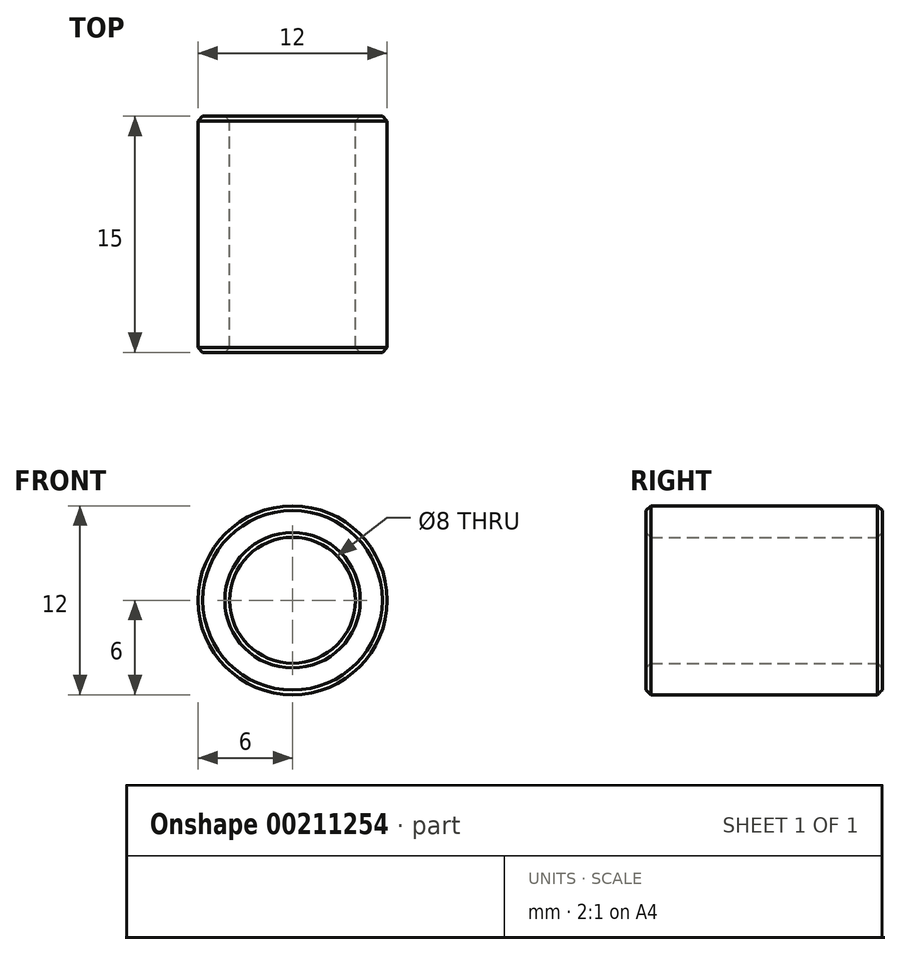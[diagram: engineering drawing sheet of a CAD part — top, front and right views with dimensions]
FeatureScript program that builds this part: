
annotation { "Feature Type Name" : "Feature", "Feature Type Description" : "" }
export const myFeature = defineFeature(function(context is Context, id is Id, definition is map)
    precondition{}
    {
        {
            var Q0;
            Q0=qCreatedBy(makeId("Front.planeOp"),FACE);
            var sketch = newSketch(context, id + "F0", { "sketchPlane" : qUnion([Q0])});
            skCircle(sketch, "E0", {"center": v(0, 0) * mm, "radius": 6 * mm});
            skCircle(sketch, "E1", {"center": v(0, 0) * mm, "radius": 4 * mm});
            skSolve(sketch);
        }
        {
            var Q0;
            Q0=makeQuery(id+"F0.imprint","IMPRINT",FACE,{"disambiguationData":[TD([[makeQuery(id+"F0.imprint","IMPRINT",EDGE,{"derivedFrom":sQuery(id+"F0.wireOp",EDGE,"E0")}),1.0]])]});
            extrude(context, id + "F1", {"entities" : qUnion([Q0]), "endBound" : BoundingType.SYMMETRIC, "depth" : 15 * mm});
        }
        {
            var Q0;
            Q0=makeQuery(id+"F1.opExtrude","CAP_FACE",FACE,{"disambiguationData":[OSD([sQuery(id+"F0.wireOp",EDGE,"E0"),sQuery(id+"F0.wireOp",EDGE,"E1")])],"isStart":false});
            var Q1;
            Q1=makeQuery(id+"F1.opExtrude","CAP_FACE",FACE,{"disambiguationData":[OSD([sQuery(id+"F0.wireOp",EDGE,"E0"),sQuery(id+"F0.wireOp",EDGE,"E1")])],"isStart":true});
            chamfer(context, id + "F2", {"entities" : qUnion([Q0, Q1]), "width" : .3 * mm, "tangentPropagation" : true});
        }
    });
